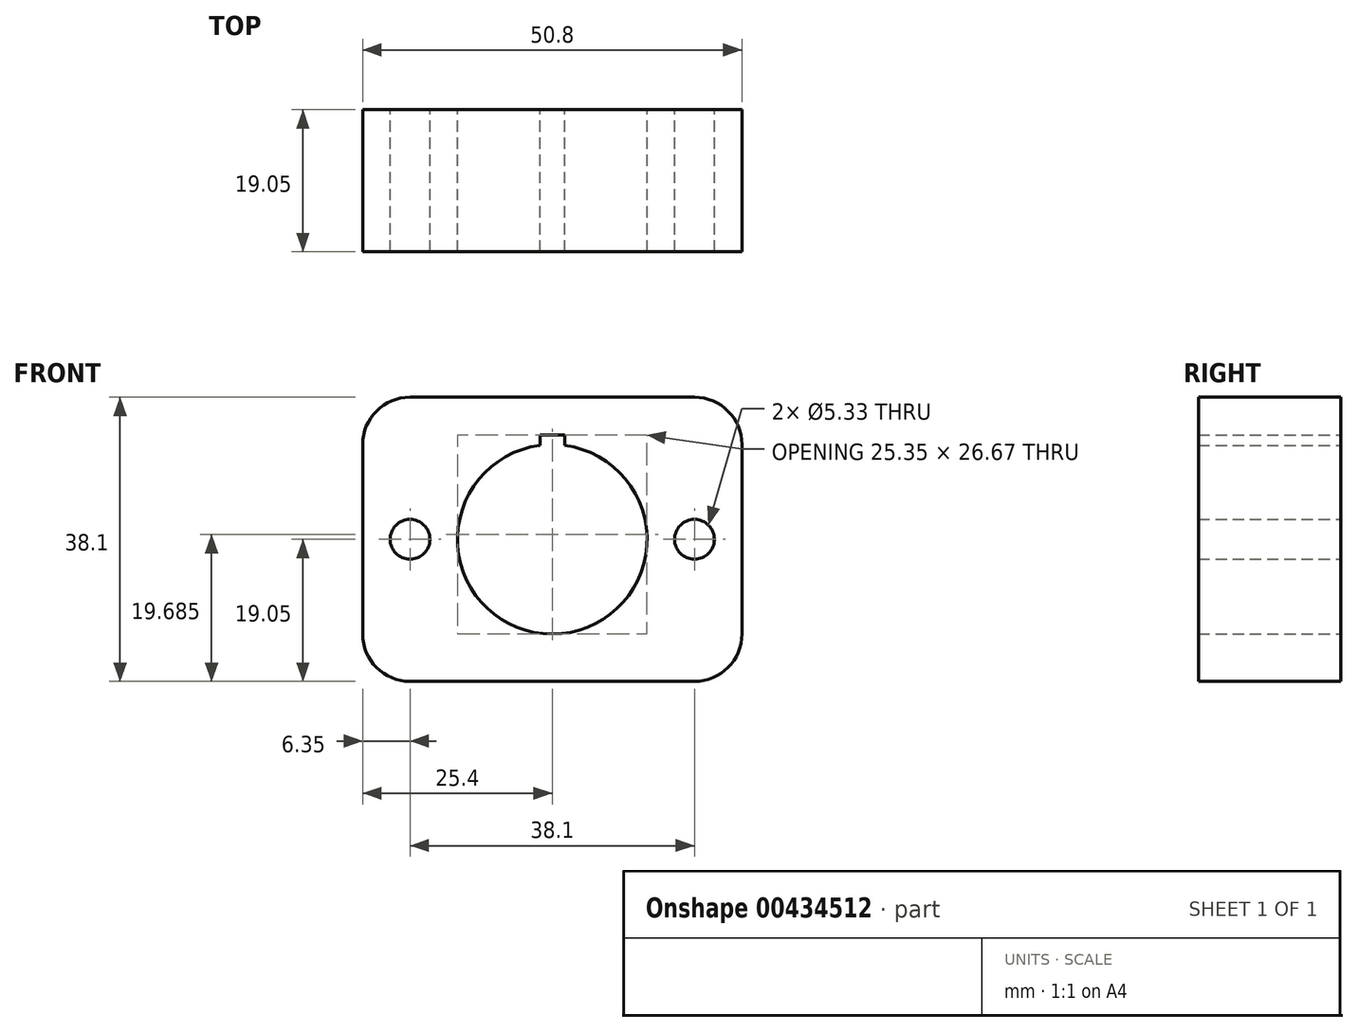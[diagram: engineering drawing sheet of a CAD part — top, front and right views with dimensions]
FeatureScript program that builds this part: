
annotation { "Feature Type Name" : "Feature", "Feature Type Description" : "" }
export const myFeature = defineFeature(function(context is Context, id is Id, definition is map)
    precondition{}
    {
        {
            var Q0;
            Q0=qCreatedBy(makeId("Front.planeOp"),FACE);
            var sketch = newSketch(context, id + "F0", { "sketchPlane" : qUnion([Q0])});
            skLineSegment(sketch, "E0.bottom", {"start": v(19.05, 19.05) * mm, "end": v(-19.05, 19.05) * mm});
            skLineSegment(sketch, "E0.top", {"start": v(19.05, -19.05) * mm, "end": v(-19.05, -19.05) * mm});
            skLineSegment(sketch, "E0.left", {"start": v(25.4, 12.7) * mm, "end": v(25.4, -12.7) * mm});
            skLineSegment(sketch, "E0.right", {"start": v(-25.4, 12.7) * mm, "end": v(-25.4, -12.7) * mm});
            skPoint(sketch, "E0.middle", {"position": v(0, 0) * mm});
            skPoint(sketch, "E1.visualSharp", {"position": v(-25.4, 19.05) * mm});
            skArc(sketch, "E1.filletArc", {"start": v(-19.05, 19.05) * mm, "mid": v(-23.54, 17.2) * mm, "end": v(-25.4, 12.7) * mm});
            skPoint(sketch, "E2.visualSharp", {"position": v(25.4, 19.05) * mm});
            skArc(sketch, "E2.filletArc", {"start": v(25.4, 12.7) * mm, "mid": v(23.54, 17.2) * mm, "end": v(19.05, 19.05) * mm});
            skPoint(sketch, "E3.visualSharp", {"position": v(25.4, -19.05) * mm});
            skArc(sketch, "E3.filletArc", {"start": v(19.05, -19.05) * mm, "mid": v(23.54, -17.2) * mm, "end": v(25.4, -12.7) * mm});
            skPoint(sketch, "E4.visualSharp", {"position": v(-25.4, -19.05) * mm});
            skArc(sketch, "E4.filletArc", {"start": v(-25.4, -12.7) * mm, "mid": v(-23.54, -17.2) * mm, "end": v(-19.05, -19.05) * mm});
            skCircle(sketch, "E5", {"center": v(0, 0) * mm, "radius": 12.7 * mm});
            skPoint(sketch, "E6", {"position": v(0, 13.97) * mm});
            skLineSegment(sketch, "E7", {"start": v(-1.65, 13.97) * mm, "end": v(1.65, 13.97) * mm});
            skLineSegment(sketch, "E8", {"start": v(-1.65, 13.97) * mm, "end": v(-1.65, 12.6) * mm});
            skLineSegment(sketch, "E9", {"start": v(1.65, 13.97) * mm, "end": v(1.65, 12.6) * mm});
            skPoint(sketch, "E10", {"position": v(19.05, 0) * mm});
            skCircle(sketch, "E11", {"center": v(19.05, 0) * mm, "radius": 2.67 * mm});
            skCircle(sketch, "E12.MirrorC", {"center": v(-19.05, 0) * mm, "radius": 2.67 * mm});
            skSolve(sketch);
        }
        {
            var Q0;
            Q0 = qSketchRegion(id + "F0", true);
            extrude(context, id + "F1", {"entities" : qUnion([Q0]), "depth" : 19.05 * mm});
        }
    });
